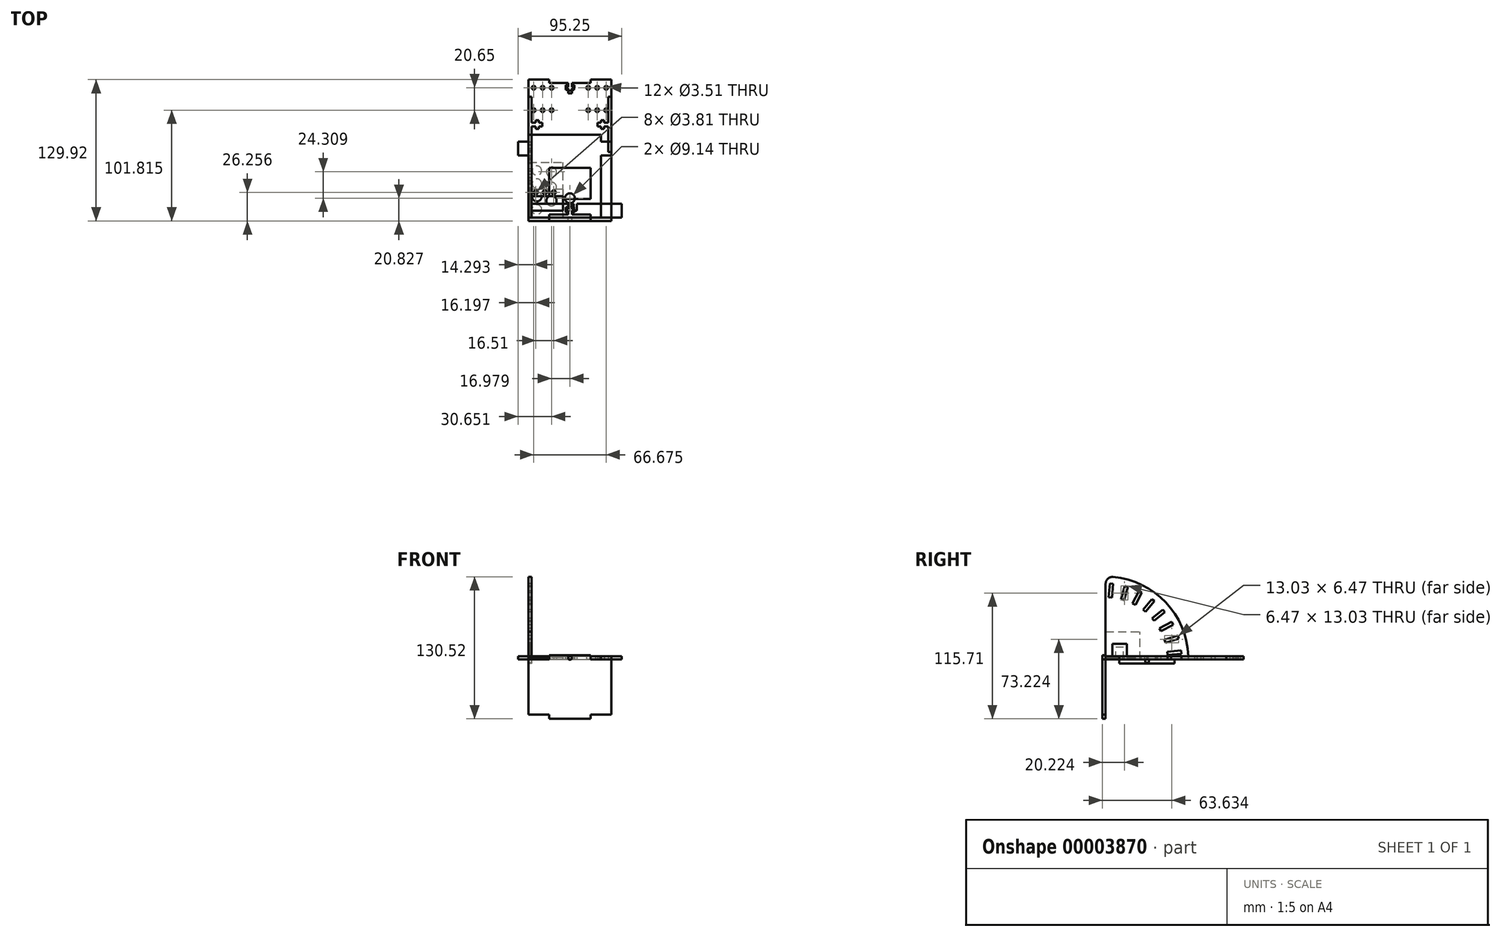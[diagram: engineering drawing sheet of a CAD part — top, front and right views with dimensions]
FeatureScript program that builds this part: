
annotation { "Feature Type Name" : "Feature", "Feature Type Description" : "" }
export const myFeature = defineFeature(function(context is Context, id is Id, definition is map)
    precondition{}
    {
        {
            var Q0;
            Q0=qCreatedBy(makeId("Right.planeOp"),FACE);
            var sketch = newSketch(context, id + "F0", { "sketchPlane" : qUnion([Q0])});
            skLineSegment(sketch, "E0", {"start": v(0, 0) * mm, "end": v(12.7, 0) * mm});
            skLineSegment(sketch, "E1", {"start": v(12.7, 0) * mm, "end": v(12.7, -3.81) * mm});
            skLineSegment(sketch, "E2", {"start": v(12.7, -3.81) * mm, "end": v(63.5, -3.81) * mm});
            skLineSegment(sketch, "E3", {"start": v(63.5, -3.81) * mm, "end": v(63.5, 0) * mm});
            skLineSegment(sketch, "E4", {"start": v(63.5, 0) * mm, "end": v(76.2, 0) * mm});
            skLineSegment(sketch, "E5", {"start": v(0, 0) * mm, "end": v(0, 69.56) * mm});
            skArc(sketch, "E6", {"start": v(76.2, 0) * mm, "mid": v(56.28, 51.37) * mm, "end": v(6.93, 75.88) * mm});
            skPoint(sketch, "E7.visualSharp", {"position": v(0, 76.2) * mm});
            skArc(sketch, "E7.filletArc", {"start": v(6.93, 75.88) * mm, "mid": v(2.07, 74.25) * mm, "end": v(0, 69.56) * mm});
            skSolve(sketch);
        }
        {
            var Q0;
            Q0=makeQuery(id+"F0.imprint","IMPRINT",FACE,{"disambiguationData":[TD([[makeQuery(id+"F0.imprint","IMPRINT",EDGE,{"derivedFrom":sQuery(id+"F0.wireOp",EDGE,"E0")}),1.0]])]});
            extrude(context, id + "F1", {"entities" : qUnion([Q0]), "depth" : 2.92 * mm});
        }
        {
            var Q0;
            Q0=qCreatedBy(makeId("Right.planeOp"),FACE);
            var sketch = newSketch(context, id + "F2", { "sketchPlane" : qUnion([Q0])});
            skLineSegment(sketch, "E8", {"start": v(56.74, 7.15) * mm, "end": v(69.4, 8.26) * mm});
            skLineSegment(sketch, "E9", {"start": v(69.4, 8.26) * mm, "end": v(69.66, 5.27) * mm});
            skLineSegment(sketch, "E10", {"start": v(69.66, 5.27) * mm, "end": v(57, 4.17) * mm});
            skLineSegment(sketch, "E11", {"start": v(57, 4.17) * mm, "end": v(56.74, 7.15) * mm});
            skLineSegment(sketch, "E12.1.0", {"start": v(54.2, 18.26) * mm, "end": v(66.38, 21.85) * mm});
            skLineSegment(sketch, "E12.1.1", {"start": v(66.38, 21.85) * mm, "end": v(67.23, 18.97) * mm});
            skLineSegment(sketch, "E12.1.2", {"start": v(67.23, 18.97) * mm, "end": v(55.05, 15.38) * mm});
            skLineSegment(sketch, "E12.1.3", {"start": v(55.05, 15.38) * mm, "end": v(54.2, 18.26) * mm});
            skLineSegment(sketch, "E12.2.0", {"start": v(49.5, 28.63) * mm, "end": v(60.74, 34.57) * mm});
            skLineSegment(sketch, "E12.2.1", {"start": v(60.74, 34.57) * mm, "end": v(62.14, 31.92) * mm});
            skLineSegment(sketch, "E12.2.2", {"start": v(62.14, 31.92) * mm, "end": v(50.9, 25.98) * mm});
            skLineSegment(sketch, "E12.2.3", {"start": v(50.9, 25.98) * mm, "end": v(49.5, 28.63) * mm});
            skLineSegment(sketch, "E12.3.0", {"start": v(42.85, 37.87) * mm, "end": v(52.68, 45.92) * mm});
            skLineSegment(sketch, "E12.3.1", {"start": v(52.68, 45.92) * mm, "end": v(54.58, 43.6) * mm});
            skLineSegment(sketch, "E12.3.2", {"start": v(54.58, 43.6) * mm, "end": v(44.75, 35.56) * mm});
            skLineSegment(sketch, "E12.3.3", {"start": v(44.75, 35.56) * mm, "end": v(42.85, 37.87) * mm});
            skLineSegment(sketch, "E12.4.0", {"start": v(34.5, 45.62) * mm, "end": v(42.54, 55.44) * mm});
            skLineSegment(sketch, "E12.4.1", {"start": v(42.54, 55.44) * mm, "end": v(44.86, 53.55) * mm});
            skLineSegment(sketch, "E12.4.2", {"start": v(44.86, 53.55) * mm, "end": v(36.82, 43.72) * mm});
            skLineSegment(sketch, "E12.4.3", {"start": v(36.82, 43.72) * mm, "end": v(34.5, 45.62) * mm});
            skLineSegment(sketch, "E12.5.0", {"start": v(24.78, 51.55) * mm, "end": v(30.71, 62.77) * mm});
            skLineSegment(sketch, "E12.5.1", {"start": v(30.71, 62.77) * mm, "end": v(33.36, 61.37) * mm});
            skLineSegment(sketch, "E12.5.2", {"start": v(33.36, 61.37) * mm, "end": v(27.43, 50.15) * mm});
            skLineSegment(sketch, "E12.5.3", {"start": v(27.43, 50.15) * mm, "end": v(24.78, 51.55) * mm});
            skLineSegment(sketch, "E12.6.0", {"start": v(14.07, 55.43) * mm, "end": v(17.66, 67.62) * mm});
            skLineSegment(sketch, "E12.6.1", {"start": v(17.66, 67.62) * mm, "end": v(20.54, 66.77) * mm});
            skLineSegment(sketch, "E12.6.2", {"start": v(20.54, 66.77) * mm, "end": v(16.95, 54.59) * mm});
            skLineSegment(sketch, "E12.6.3", {"start": v(16.95, 54.59) * mm, "end": v(14.07, 55.43) * mm});
            skLineSegment(sketch, "E12.7.0", {"start": v(2.8, 57.12) * mm, "end": v(3.91, 69.77) * mm});
            skLineSegment(sketch, "E12.7.1", {"start": v(3.91, 69.77) * mm, "end": v(6.9, 69.51) * mm});
            skLineSegment(sketch, "E12.7.2", {"start": v(6.9, 69.51) * mm, "end": v(5.8, 56.86) * mm});
            skLineSegment(sketch, "E12.7.3", {"start": v(5.8, 56.86) * mm, "end": v(2.8, 57.12) * mm});
            skPoint(sketch, "E12.center", {"position": v(0, 0) * mm});
            skLineSegment(sketch, "E12.anchor1", {"start": v(0, 0) * mm, "end": v(56.74, 7.15) * mm, "construction": true});
            skLineSegment(sketch, "E12.anchor2", {"start": v(0, 0) * mm, "end": v(2.8, 57.12) * mm, "construction": true});
            skCircle(sketch, "E13", {"center": v(0, 0) * mm, "radius": 69.85 * mm, "construction": true});
            skCircle(sketch, "E14", {"center": v(0, 0) * mm, "radius": 57.15 * mm, "construction": true});
            skCircle(sketch, "E15", {"center": v(38.1, -1.46) * mm, "radius": 1.75 * mm});
            skSolve(sketch);
        }
        {
            var Q0;
            {Q0=qUnion([makeQuery(id+"F2.imprint","IMPRINT",FACE,{"disambiguationData":[TD([[makeQuery(id+"F2.imprint","IMPRINT",EDGE,{"derivedFrom":sQuery(id+"F2.wireOp",EDGE,"E8")}),-1.0]])]}),makeQuery(id+"F2.imprint","IMPRINT",FACE,{"disambiguationData":[TD([[makeQuery(id+"F2.imprint","IMPRINT",EDGE,{"derivedFrom":sQuery(id+"F2.wireOp",EDGE,"E12.1.0")}),-1.0]])]}),makeQuery(id+"F2.imprint","IMPRINT",FACE,{"disambiguationData":[TD([[makeQuery(id+"F2.imprint","IMPRINT",EDGE,{"derivedFrom":sQuery(id+"F2.wireOp",EDGE,"E12.2.0")}),-1.0]])]}),makeQuery(id+"F2.imprint","IMPRINT",FACE,{"disambiguationData":[TD([[makeQuery(id+"F2.imprint","IMPRINT",EDGE,{"derivedFrom":sQuery(id+"F2.wireOp",EDGE,"E12.3.0")}),-1.0]])]}),makeQuery(id+"F2.imprint","IMPRINT",FACE,{"disambiguationData":[TD([[makeQuery(id+"F2.imprint","IMPRINT",EDGE,{"derivedFrom":sQuery(id+"F2.wireOp",EDGE,"E12.4.0")}),-1.0]])]}),makeQuery(id+"F2.imprint","IMPRINT",FACE,{"disambiguationData":[TD([[makeQuery(id+"F2.imprint","IMPRINT",EDGE,{"derivedFrom":sQuery(id+"F2.wireOp",EDGE,"E12.5.0")}),-1.0]])]}),makeQuery(id+"F2.imprint","IMPRINT",FACE,{"disambiguationData":[TD([[makeQuery(id+"F2.imprint","IMPRINT",EDGE,{"derivedFrom":sQuery(id+"F2.wireOp",EDGE,"E12.6.0")}),-1.0]])]}),makeQuery(id+"F2.imprint","IMPRINT",FACE,{"disambiguationData":[TD([[makeQuery(id+"F2.imprint","IMPRINT",EDGE,{"derivedFrom":sQuery(id+"F2.wireOp",EDGE,"E12.7.0")}),-1.0]])]}),makeQuery(id+"F2.imprint","IMPRINT",FACE,{"disambiguationData":[TD([[makeQuery(id+"F2.imprint","IMPRINT",EDGE,{"derivedFrom":sQuery(id+"F2.wireOp",EDGE,"E15")}),1.0]])]})]);}
            extrude(context, id + "F3", {"entities" : qUnion([Q0]), "operationType" : NewBodyOperationType.REMOVE, "depth" : 25.4 * mm});
        }
        {
            var Q0;
            Q0=qCreatedBy(makeId("Top.planeOp"),FACE);
            var sketch = newSketch(context, id + "F4", { "sketchPlane" : qUnion([Q0])});
            skLineSegment(sketch, "E16", {"start": v(0, 127) * mm, "end": v(0, 111.13) * mm});
            skLineSegment(sketch, "E17", {"start": v(0, 111.13) * mm, "end": v(2.92, 111.13) * mm});
            skLineSegment(sketch, "E18", {"start": v(2.92, 111.12) * mm, "end": v(2.92, 87.48) * mm});
            skLineSegment(sketch, "E19", {"start": v(2.92, 87.48) * mm, "end": v(6.75, 87.48) * mm});
            skLineSegment(sketch, "E20", {"start": v(6.75, 87.48) * mm, "end": v(6.75, 89.66) * mm});
            skLineSegment(sketch, "E21", {"start": v(6.75, 89.66) * mm, "end": v(9.53, 89.66) * mm});
            skLineSegment(sketch, "E22", {"start": v(9.53, 89.66) * mm, "end": v(9.53, 87.48) * mm});
            skLineSegment(sketch, "E23", {"start": v(9.53, 87.48) * mm, "end": v(12.7, 87.48) * mm});
            skLineSegment(sketch, "E24", {"start": v(12.7, 87.48) * mm, "end": v(12.7, 83.97) * mm});
            skLineSegment(sketch, "E25.0.MirrorCS", {"start": v(0, 60.33) * mm, "end": v(2.92, 60.33) * mm});
            skLineSegment(sketch, "E26.0.MirrorCS", {"start": v(2.92, 60.33) * mm, "end": v(2.92, 83.97) * mm});
            skLineSegment(sketch, "E27.0.MirrorCS", {"start": v(2.92, 83.97) * mm, "end": v(6.75, 83.97) * mm});
            skLineSegment(sketch, "E28.0.MirrorCS", {"start": v(6.75, 83.97) * mm, "end": v(6.75, 81.79) * mm});
            skLineSegment(sketch, "E29.0.MirrorCS", {"start": v(6.75, 81.79) * mm, "end": v(9.52, 81.79) * mm});
            skLineSegment(sketch, "E30.0.MirrorCS", {"start": v(9.52, 81.79) * mm, "end": v(9.52, 83.97) * mm});
            skLineSegment(sketch, "E31.0.MirrorCS", {"start": v(9.52, 83.97) * mm, "end": v(12.7, 83.97) * mm});
            skLineSegment(sketch, "E32.0.MirrorCS", {"start": v(76.2, 127) * mm, "end": v(76.2, 111.13) * mm});
            skLineSegment(sketch, "E33.0.MirrorCS", {"start": v(76.2, 111.13) * mm, "end": v(73.28, 111.13) * mm});
            skLineSegment(sketch, "E34.0.MirrorCS", {"start": v(73.28, 111.13) * mm, "end": v(73.28, 87.48) * mm});
            skLineSegment(sketch, "E35.0.MirrorCS", {"start": v(73.28, 87.48) * mm, "end": v(69.45, 87.48) * mm});
            skLineSegment(sketch, "E36.0.MirrorCS", {"start": v(69.45, 87.48) * mm, "end": v(69.45, 89.66) * mm});
            skLineSegment(sketch, "E37.0.MirrorCS", {"start": v(69.45, 89.66) * mm, "end": v(66.68, 89.66) * mm});
            skLineSegment(sketch, "E38.0.MirrorCS", {"start": v(66.67, 89.66) * mm, "end": v(66.67, 87.48) * mm});
            skLineSegment(sketch, "E39.0.MirrorCS", {"start": v(66.67, 87.48) * mm, "end": v(63.5, 87.48) * mm});
            skLineSegment(sketch, "E40.0.MirrorCS", {"start": v(63.5, 83.97) * mm, "end": v(63.5, 87.48) * mm});
            skLineSegment(sketch, "E41.0.MirrorCS", {"start": v(66.68, 83.97) * mm, "end": v(63.5, 83.97) * mm});
            skLineSegment(sketch, "E42.0.MirrorCS", {"start": v(66.68, 81.79) * mm, "end": v(66.68, 83.97) * mm});
            skLineSegment(sketch, "E43.0.MirrorCS", {"start": v(69.45, 81.79) * mm, "end": v(66.68, 81.79) * mm});
            skLineSegment(sketch, "E44.0.MirrorCS", {"start": v(69.45, 83.97) * mm, "end": v(69.45, 81.79) * mm});
            skLineSegment(sketch, "E45.0.MirrorCS", {"start": v(73.28, 83.97) * mm, "end": v(69.45, 83.97) * mm});
            skLineSegment(sketch, "E46.0.MirrorCS", {"start": v(73.28, 60.33) * mm, "end": v(73.28, 83.97) * mm});
            skLineSegment(sketch, "E47.0.MirrorCS", {"start": v(76.2, 60.33) * mm, "end": v(73.28, 60.33) * mm});
            skLineSegment(sketch, "E48", {"start": v(0, 0) * mm, "end": v(75.06, 0) * mm, "construction": true});
            skLineSegment(sketch, "E49", {"start": v(0, 127) * mm, "end": v(76.2, 127) * mm, "construction": true});
            skLineSegment(sketch, "E50", {"start": v(19.05, 0) * mm, "end": v(19.05, 2.92) * mm});
            skLineSegment(sketch, "E51", {"start": v(19.05, 2.92) * mm, "end": v(36.35, 2.92) * mm});
            skLineSegment(sketch, "E52", {"start": v(36.35, 2.92) * mm, "end": v(36.35, 6.75) * mm});
            skLineSegment(sketch, "E53", {"start": v(36.35, 6.75) * mm, "end": v(34.16, 6.75) * mm});
            skLineSegment(sketch, "E54", {"start": v(34.16, 6.75) * mm, "end": v(34.16, 9.53) * mm});
            skLineSegment(sketch, "E55", {"start": v(34.16, 9.53) * mm, "end": v(36.35, 9.53) * mm});
            skLineSegment(sketch, "E56", {"start": v(36.35, 9.53) * mm, "end": v(36.35, 12.7) * mm});
            skLineSegment(sketch, "E57.0.MirrorCS", {"start": v(57.15, 0) * mm, "end": v(57.15, 2.92) * mm});
            skLineSegment(sketch, "E58.0.MirrorCS", {"start": v(57.15, 2.92) * mm, "end": v(39.85, 2.92) * mm});
            skLineSegment(sketch, "E59.0.MirrorCS", {"start": v(39.85, 2.8) * mm, "end": v(39.85, 2.92) * mm});
            skLineSegment(sketch, "E60.0.MirrorCS", {"start": v(19.05, 127) * mm, "end": v(19.05, 124.08) * mm});
            skLineSegment(sketch, "E61.0.MirrorCS", {"start": v(19.05, 124.08) * mm, "end": v(36.35, 124.08) * mm});
            skLineSegment(sketch, "E62.0.MirrorCS", {"start": v(0, 127) * mm, "end": v(19.05, 127) * mm});
            skLineSegment(sketch, "E63.0.MirrorCS", {"start": v(36.35, 124.08) * mm, "end": v(36.35, 120.25) * mm});
            skLineSegment(sketch, "E64.0.MirrorCS", {"start": v(36.35, 120.25) * mm, "end": v(34.16, 120.25) * mm});
            skLineSegment(sketch, "E65.0.MirrorCS", {"start": v(34.16, 120.25) * mm, "end": v(34.16, 117.48) * mm});
            skLineSegment(sketch, "E66.0.MirrorCS", {"start": v(34.16, 117.48) * mm, "end": v(36.35, 117.48) * mm});
            skLineSegment(sketch, "E67.0.MirrorCS", {"start": v(36.35, 117.48) * mm, "end": v(36.35, 114.3) * mm});
            skLineSegment(sketch, "E68.0.MirrorCS", {"start": v(36.35, 114.3) * mm, "end": v(39.85, 114.3) * mm});
            skLineSegment(sketch, "E69.0.MirrorCS", {"start": v(39.85, 117.48) * mm, "end": v(39.85, 114.3) * mm});
            skLineSegment(sketch, "E70.0.MirrorCS", {"start": v(42.04, 117.48) * mm, "end": v(39.85, 117.48) * mm});
            skLineSegment(sketch, "E71.0.MirrorCS", {"start": v(42.04, 120.25) * mm, "end": v(42.04, 117.48) * mm});
            skLineSegment(sketch, "E72.0.MirrorCS", {"start": v(39.85, 120.25) * mm, "end": v(42.04, 120.25) * mm});
            skLineSegment(sketch, "E73.0.MirrorCS", {"start": v(39.85, 124.08) * mm, "end": v(39.85, 120.25) * mm});
            skLineSegment(sketch, "E74.0.MirrorCS", {"start": v(57.15, 124.08) * mm, "end": v(39.85, 124.08) * mm});
            skLineSegment(sketch, "E75.0.MirrorCS", {"start": v(57.15, 127) * mm, "end": v(57.15, 124.08) * mm});
            skLineSegment(sketch, "E76", {"start": v(57.15, 127) * mm, "end": v(76.2, 127) * mm});
            skLineSegment(sketch, "E77", {"start": v(39.85, 2.92) * mm, "end": v(39.85, 6.75) * mm});
            skLineSegment(sketch, "E78", {"start": v(39.85, 6.75) * mm, "end": v(42.04, 6.75) * mm});
            skLineSegment(sketch, "E79", {"start": v(42.04, 6.75) * mm, "end": v(42.04, 9.53) * mm});
            skLineSegment(sketch, "E80", {"start": v(42.04, 9.53) * mm, "end": v(39.85, 9.53) * mm});
            skLineSegment(sketch, "E81", {"start": v(39.85, 9.53) * mm, "end": v(39.85, 12.7) * mm});
            skLineSegment(sketch, "E82", {"start": v(39.85, 12.7) * mm, "end": v(36.35, 12.7) * mm});
            skLineSegment(sketch, "E83", {"start": v(76.2, 60.33) * mm, "end": v(76.2, 0) * mm});
            skLineSegment(sketch, "E84", {"start": v(76.2, 0) * mm, "end": v(57.15, 0) * mm});
            skLineSegment(sketch, "E85", {"start": v(19.05, 0) * mm, "end": v(0, 0) * mm});
            skLineSegment(sketch, "E86", {"start": v(0, 60.33) * mm, "end": v(0, 0) * mm});
            skLineSegment(sketch, "E87.bottom", {"start": v(19.05, 45.72) * mm, "end": v(57.15, 45.72) * mm});
            skLineSegment(sketch, "E87.top", {"start": v(19.05, 17.14) * mm, "end": v(57.15, 17.14) * mm});
            skLineSegment(sketch, "E87.left", {"start": v(19.05, 45.72) * mm, "end": v(19.05, 17.14) * mm});
            skLineSegment(sketch, "E87.right", {"start": v(57.15, 45.72) * mm, "end": v(57.15, 17.14) * mm});
            skSolve(sketch);
        }
        {
            var Q0;
            Q0 = qSketchRegion(id + "F4", true);
            extrude(context, id + "F5", {"entities" : qUnion([Q0]), "depth" : 2.92 * mm});
        }
        {
            var Q0;
            Q0=qCreatedBy(makeId("Top.planeOp"),FACE);
            var sketch = newSketch(context, id + "F6", { "sketchPlane" : qUnion([Q0])});
            skLineSegment(sketch, "E88", {"start": v(0, 0) * mm, "end": v(0, 57.15) * mm});
            skLineSegment(sketch, "E89", {"start": v(0, 57.15) * mm, "end": v(-9.53, 57.15) * mm});
            skLineSegment(sketch, "E90", {"start": v(-9.53, 57.15) * mm, "end": v(-9.53, 69.85) * mm});
            skLineSegment(sketch, "E91", {"start": v(-9.53, 69.85) * mm, "end": v(0, 69.85) * mm});
            skLineSegment(sketch, "E92", {"start": v(0, 69.85) * mm, "end": v(0, 76.2) * mm});
            skLineSegment(sketch, "E93", {"start": v(0, 76.2) * mm, "end": v(66.68, 76.2) * mm});
            skLineSegment(sketch, "E94", {"start": v(0, 0) * mm, "end": v(66.68, 0) * mm});
            skLineSegment(sketch, "E95", {"start": v(33.34, 93.53) * mm, "end": v(33.34, 0) * mm, "construction": true});
            skLineSegment(sketch, "E96.0.MirrorCS", {"start": v(66.68, 69.85) * mm, "end": v(66.68, 76.2) * mm});
            skLineSegment(sketch, "E97.0.MirrorCS", {"start": v(76.2, 69.85) * mm, "end": v(66.68, 69.85) * mm});
            skLineSegment(sketch, "E98.0.MirrorCS", {"start": v(76.2, 57.15) * mm, "end": v(76.2, 69.85) * mm});
            skLineSegment(sketch, "E99.0.MirrorCS", {"start": v(66.68, 57.15) * mm, "end": v(76.2, 57.15) * mm});
            skLineSegment(sketch, "E100.0.MirrorCS", {"start": v(66.68, 0) * mm, "end": v(66.68, 57.15) * mm});
            skSolve(sketch);
        }
        {
            var Q0;
            Q0=makeQuery(id+"F6.imprint","IMPRINT",FACE,{"disambiguationData":[TD([[makeQuery(id+"F6.imprint","IMPRINT",EDGE,{"derivedFrom":sQuery(id+"F6.wireOp",EDGE,"E88")}),-1.0]])]});
            extrude(context, id + "F7", {"entities" : qUnion([Q0]), "depth" : 2.92 * mm});
        }
        {
            var Q0;
            Q0=qCreatedBy(makeId("Front.planeOp"),FACE);
            var sketch = newSketch(context, id + "F8", { "sketchPlane" : qUnion([Q0])});
            skLineSegment(sketch, "E101", {"start": v(0, 0) * mm, "end": v(19.05, 0) * mm});
            skLineSegment(sketch, "E102", {"start": v(19.05, 0) * mm, "end": v(19.05, 3.81) * mm});
            skLineSegment(sketch, "E103", {"start": v(19.05, 3.81) * mm, "end": v(57.15, 3.81) * mm});
            skLineSegment(sketch, "E104", {"start": v(57.15, 3.81) * mm, "end": v(57.15, 0) * mm});
            skLineSegment(sketch, "E105", {"start": v(57.15, 0) * mm, "end": v(76.2, 0) * mm});
            skLineSegment(sketch, "E106", {"start": v(76.2, 0) * mm, "end": v(76.2, -50.8) * mm});
            skLineSegment(sketch, "E107", {"start": v(76.2, -50.8) * mm, "end": v(57.15, -50.8) * mm});
            skLineSegment(sketch, "E108", {"start": v(57.15, -50.8) * mm, "end": v(57.15, -54.6) * mm});
            skLineSegment(sketch, "E109", {"start": v(57.15, -54.6) * mm, "end": v(19.05, -54.6) * mm});
            skLineSegment(sketch, "E110", {"start": v(19.05, -54.6) * mm, "end": v(19.05, -50.8) * mm});
            skLineSegment(sketch, "E111", {"start": v(19.05, -50.8) * mm, "end": v(0, -50.8) * mm});
            skLineSegment(sketch, "E112", {"start": v(0, -50.8) * mm, "end": v(0, 0) * mm});
            skSolve(sketch);
        }
        {
            var Q0;
            Q0=makeQuery(id+"F8.imprint","IMPRINT",FACE,{"disambiguationData":[TD([[makeQuery(id+"F8.imprint","IMPRINT",EDGE,{"derivedFrom":sQuery(id+"F8.wireOp",EDGE,"E101")}),-1.0]])]});
            extrude(context, id + "F9", {"entities" : qUnion([Q0]), "depth" : 2.92 * mm});
        }
        {
            var Q0;
            Q0=qCreatedBy(makeId("Front.planeOp"),FACE);
            var sketch = newSketch(context, id + "F10", { "sketchPlane" : qUnion([Q0])});
            skCircle(sketch, "E113", {"center": v(38.1, 1.46) * mm, "radius": 1.75 * mm});
            skLineSegment(sketch, "E114", {"start": v(-12.64, -25.4) * mm, "end": v(76.2, -25.4) * mm, "construction": true});
            skCircle(sketch, "E115.0.MirrorC", {"center": v(38.1, -52.26) * mm, "radius": 1.75 * mm});
            skSolve(sketch);
        }
        {
            var Q0;
            {Q0=qUnion([makeQuery(id+"F10.imprint","IMPRINT",FACE,{"disambiguationData":[TD([[makeQuery(id+"F10.imprint","IMPRINT",EDGE,{"derivedFrom":sQuery(id+"F10.wireOp",EDGE,"E113")}),1.0]])]}),makeQuery(id+"F10.imprint","IMPRINT",FACE,{"disambiguationData":[TD([[makeQuery(id+"F10.imprint","IMPRINT",EDGE,{"derivedFrom":sQuery(id+"F10.wireOp",EDGE,"E115.0.MirrorC")}),-1.0]])]})]);}
            extrude(context, id + "F11", {"entities" : qUnion([Q0]), "operationType" : NewBodyOperationType.REMOVE, "depth" : 25.4 * mm});
        }
        {
            var Q0;
            Q0=qCreatedBy(makeId("Top.planeOp"),FACE);
            var sketch = newSketch(context, id + "F12", { "sketchPlane" : qUnion([Q0])});
            skLineSegment(sketch, "E116", {"start": v(0, 0) * mm, "end": v(19.05, 0) * mm});
            skLineSegment(sketch, "E117", {"start": v(19.05, 0) * mm, "end": v(19.05, 2.92) * mm});
            skLineSegment(sketch, "E118", {"start": v(19.05, 2.92) * mm, "end": v(36.35, 2.92) * mm});
            skLineSegment(sketch, "E119", {"start": v(36.35, 2.92) * mm, "end": v(36.35, 5) * mm});
            skLineSegment(sketch, "E120", {"start": v(36.35, 5) * mm, "end": v(34.13, 5) * mm});
            skLineSegment(sketch, "E121", {"start": v(34.13, 5) * mm, "end": v(34.13, 7.78) * mm});
            skLineSegment(sketch, "E122", {"start": v(34.13, 7.78) * mm, "end": v(36.35, 7.78) * mm});
            skLineSegment(sketch, "E123", {"start": v(36.35, 7.78) * mm, "end": v(36.35, 10.16) * mm});
            skLineSegment(sketch, "E124", {"start": v(36.35, 10.16) * mm, "end": v(38.1, 10.16) * mm});
            skLineSegment(sketch, "E125", {"start": v(0, 0) * mm, "end": v(0, 127) * mm});
            skLineSegment(sketch, "E126", {"start": v(38.1, 63.6) * mm, "end": v(38.1, -23.35) * mm, "construction": true});
            skLineSegment(sketch, "E127.0.MirrorCS", {"start": v(39.85, 10.16) * mm, "end": v(38.1, 10.16) * mm});
            skLineSegment(sketch, "E128.0.MirrorCS", {"start": v(39.85, 7.78) * mm, "end": v(39.85, 10.16) * mm});
            skLineSegment(sketch, "E129.0.MirrorCS", {"start": v(42.07, 7.78) * mm, "end": v(39.85, 7.78) * mm});
            skLineSegment(sketch, "E130.0.MirrorCS", {"start": v(42.07, 5) * mm, "end": v(42.07, 7.78) * mm});
            skLineSegment(sketch, "E131.0.MirrorCS", {"start": v(39.85, 5) * mm, "end": v(42.07, 5) * mm});
            skLineSegment(sketch, "E132.0.MirrorCS", {"start": v(39.85, 2.92) * mm, "end": v(39.85, 5) * mm});
            skLineSegment(sketch, "E133.0.MirrorCS", {"start": v(57.15, 2.92) * mm, "end": v(39.85, 2.92) * mm});
            skLineSegment(sketch, "E134.0.MirrorCS", {"start": v(57.15, 0) * mm, "end": v(57.15, 2.92) * mm});
            skLineSegment(sketch, "E135.0.MirrorCS", {"start": v(76.2, 0) * mm, "end": v(57.15, 0) * mm});
            skLineSegment(sketch, "E136.0.MirrorCS", {"start": v(76.2, 0) * mm, "end": v(76.2, 127) * mm});
            skLineSegment(sketch, "E137", {"start": v(0, 127) * mm, "end": v(19.05, 127) * mm});
            skLineSegment(sketch, "E138", {"start": v(19.05, 127) * mm, "end": v(19.05, 124.08) * mm});
            skLineSegment(sketch, "E139", {"start": v(19.05, 124.08) * mm, "end": v(36.35, 124.08) * mm});
            skLineSegment(sketch, "E140", {"start": v(36.35, 124.08) * mm, "end": v(36.35, 122) * mm});
            skLineSegment(sketch, "E141", {"start": v(36.35, 122) * mm, "end": v(34.13, 122) * mm});
            skLineSegment(sketch, "E142", {"start": v(34.13, 122) * mm, "end": v(34.13, 119.22) * mm});
            skLineSegment(sketch, "E143", {"start": v(34.13, 119.22) * mm, "end": v(36.35, 119.22) * mm});
            skLineSegment(sketch, "E144", {"start": v(36.35, 119.22) * mm, "end": v(36.35, 116.84) * mm});
            skLineSegment(sketch, "E145", {"start": v(36.35, 116.84) * mm, "end": v(38.1, 116.84) * mm});
            skLineSegment(sketch, "E146", {"start": v(38.1, 116.84) * mm, "end": v(39.85, 116.84) * mm});
            skLineSegment(sketch, "E147", {"start": v(39.85, 116.84) * mm, "end": v(39.85, 119.22) * mm});
            skLineSegment(sketch, "E148", {"start": v(39.85, 119.22) * mm, "end": v(42.07, 119.22) * mm});
            skLineSegment(sketch, "E149", {"start": v(42.07, 119.22) * mm, "end": v(42.07, 122) * mm});
            skLineSegment(sketch, "E150", {"start": v(42.07, 122) * mm, "end": v(39.85, 122) * mm});
            skLineSegment(sketch, "E151", {"start": v(39.85, 122) * mm, "end": v(39.85, 124.08) * mm});
            skLineSegment(sketch, "E152", {"start": v(39.85, 124.08) * mm, "end": v(57.15, 124.08) * mm});
            skLineSegment(sketch, "E153", {"start": v(57.15, 124.08) * mm, "end": v(57.15, 127) * mm});
            skLineSegment(sketch, "E154", {"start": v(57.15, 127) * mm, "end": v(76.2, 127) * mm});
            skCircle(sketch, "E155", {"center": v(71.44, 119.55) * mm, "radius": 1.75 * mm});
            skCircle(sketch, "E156", {"center": v(71.44, 98.9) * mm, "radius": 1.75 * mm});
            skLineSegment(sketch, "E157", {"start": v(71.44, 119.55) * mm, "end": v(71.44, 98.9) * mm, "construction": true});
            skLineSegment(sketch, "E158", {"start": v(76.2, 109.22) * mm, "end": v(71.44, 109.22) * mm, "construction": true});
            skCircle(sketch, "E159.1.0.0", {"center": v(63.18, 119.55) * mm, "radius": 1.75 * mm});
            skCircle(sketch, "E159.1.0.1", {"center": v(63.18, 98.9) * mm, "radius": 1.75 * mm});
            skCircle(sketch, "E159.2.0.0", {"center": v(54.93, 119.55) * mm, "radius": 1.75 * mm});
            skCircle(sketch, "E159.2.0.1", {"center": v(54.93, 98.9) * mm, "radius": 1.75 * mm});
            skLineSegment(sketch, "E159.direction1", {"start": v(71.44, 119.55) * mm, "end": v(63.18, 119.55) * mm, "construction": true});
            skCircle(sketch, "E160.0.MirrorC", {"center": v(21.27, 119.55) * mm, "radius": 1.75 * mm});
            skCircle(sketch, "E161.0.MirrorC", {"center": v(13.02, 119.55) * mm, "radius": 1.75 * mm});
            skCircle(sketch, "E162.0.MirrorC", {"center": v(4.76, 119.55) * mm, "radius": 1.75 * mm});
            skCircle(sketch, "E163.0.MirrorC", {"center": v(4.76, 98.9) * mm, "radius": 1.75 * mm});
            skCircle(sketch, "E164.0.MirrorC", {"center": v(13.02, 98.9) * mm, "radius": 1.75 * mm});
            skCircle(sketch, "E165.0.MirrorC", {"center": v(21.27, 98.9) * mm, "radius": 1.75 * mm});
            skCircle(sketch, "E166", {"center": v(38.1, 17.9) * mm, "radius": 4.57 * mm});
            skSolve(sketch);
        }
        {
            var Q0;
            Q0 = qSketchRegion(id + "F12", true);
            extrude(context, id + "F13", {"entities" : qUnion([Q0]), "depth" : 2.92 * mm});
        }
        {
            var Q0;
            Q0=qCreatedBy(makeId("Right.planeOp"),FACE);
            var sketch = newSketch(context, id + "F14", { "sketchPlane" : qUnion([Q0])});
            skLineSegment(sketch, "E167", {"start": v(0, 1.59) * mm, "end": v(6.35, 1.59) * mm});
            skLineSegment(sketch, "E168", {"start": v(6.35, 1.59) * mm, "end": v(6.35, 14.29) * mm});
            skLineSegment(sketch, "E169", {"start": v(6.35, 14.29) * mm, "end": v(19.68, 14.29) * mm});
            skLineSegment(sketch, "E170", {"start": v(19.68, 14.29) * mm, "end": v(19.69, 1.59) * mm});
            skLineSegment(sketch, "E171", {"start": v(19.69, 1.59) * mm, "end": v(26.04, 1.59) * mm});
            skLineSegment(sketch, "E172", {"start": v(26.04, 1.59) * mm, "end": v(26.04, 0) * mm});
            skLineSegment(sketch, "E173", {"start": v(26.04, 0) * mm, "end": v(0, 0) * mm});
            skLineSegment(sketch, "E174", {"start": v(0, 0) * mm, "end": v(0, 1.59) * mm});
            skSolve(sketch);
        }
        {
            var Q0;
            Q0=makeQuery(id+"F14.imprint","IMPRINT",FACE,{"disambiguationData":[TD([[makeQuery(id+"F14.imprint","IMPRINT",EDGE,{"derivedFrom":sQuery(id+"F14.wireOp",EDGE,"E167")}),-1.0]])]});
            extrude(context, id + "F15", {"entities" : qUnion([Q0]), "depth" : (0.97 + (1 / 8)) * mm});
        }
        {
            var Q0;
            Q0=qCreatedBy(makeId("Top.planeOp"),FACE);
            var sketch = newSketch(context, id + "F16", { "sketchPlane" : qUnion([Q0])});
            skLineSegment(sketch, "E175.bottom", {"start": v(1.59, 18.1) * mm, "end": v(26.35, 18.1) * mm});
            skLineSegment(sketch, "E175.top", {"start": v(1.59, 7.94) * mm, "end": v(26.35, 7.94) * mm});
            skLineSegment(sketch, "E175.left", {"start": v(1.59, 18.1) * mm, "end": v(1.59, 7.94) * mm});
            skLineSegment(sketch, "E175.right", {"start": v(26.35, 18.1) * mm, "end": v(26.35, 7.94) * mm});
            skSolve(sketch);
        }
        {
            var Q0;
            Q0=makeQuery(id+"F16.imprint","IMPRINT",FACE,{"disambiguationData":[TD([[makeQuery(id+"F16.imprint","IMPRINT",EDGE,{"derivedFrom":sQuery(id+"F16.wireOp",EDGE,"E175.bottom")}),-1.0]])]});
            extrude(context, id + "F17", {"entities" : qUnion([Q0]), "operationType" : NewBodyOperationType.REMOVE, "depth" : 12.7 * mm});
        }
        {
            var Q0;
            Q0=qCreatedBy(makeId("Right.planeOp"),FACE);
            var sketch = newSketch(context, id + "F18", { "sketchPlane" : qUnion([Q0])});
            skLineSegment(sketch, "E176", {"start": v(11.11, 0) * mm, "end": v(14.92, 0) * mm});
            skLineSegment(sketch, "E177", {"start": v(14.92, 0) * mm, "end": v(14.92, 6.35) * mm});
            skLineSegment(sketch, "E178", {"start": v(11.11, 0) * mm, "end": v(11.11, 6.35) * mm});
            skArc(sketch, "E179", {"start": v(11.11, 6.35) * mm, "mid": v(13.02, 8.26) * mm, "end": v(14.92, 6.35) * mm});
            skLineSegment(sketch, "E180", {"start": v(6.35, 6.35) * mm, "end": v(19.69, 6.35) * mm, "construction": true});
            skLineSegment(sketch, "E181", {"start": v(4.37, 8.26) * mm, "end": v(24.9, 8.26) * mm, "construction": true});
            skSolve(sketch);
        }
        {
            var Q0;
            Q0=makeQuery(id+"F18.imprint","IMPRINT",FACE,{"disambiguationData":[TD([[makeQuery(id+"F18.imprint","IMPRINT",EDGE,{"derivedFrom":sQuery(id+"F18.wireOp",EDGE,"E176")}),1.0]])]});
            var Q1;
            Q1=makeQuery(id+"F15.opExtrude","CAP_FACE",FACE,{"disambiguationData":[OSD([sQuery(id+"F14.wireOp",EDGE,"E167"),sQuery(id+"F14.wireOp",EDGE,"E168"),sQuery(id+"F14.wireOp",EDGE,"E169"),sQuery(id+"F14.wireOp",EDGE,"E170"),sQuery(id+"F14.wireOp",EDGE,"E171"),sQuery(id+"F14.wireOp",EDGE,"E172"),sQuery(id+"F14.wireOp",EDGE,"E173"),sQuery(id+"F14.wireOp",EDGE,"E174")])],"isStart":false});
            extrude(context, id + "F19", {"entities" : qUnion([Q0, Q1]), "operationType" : NewBodyOperationType.REMOVE, "depth" : 30.48 * mm});
        }
        {
            var Q0;
            Q0=qCreatedBy(makeId("Top.planeOp"),FACE);
            var sketch = newSketch(context, id + "F20", { "sketchPlane" : qUnion([Q0])});
            skCircle(sketch, "E182", {"center": v(23.18, 23.34) * mm, "radius": 1.9 * mm});
            skLineSegment(sketch, "E183", {"start": v(0, 23.34) * mm, "end": v(27.94, 23.34) * mm, "construction": true});
            skLineSegment(sketch, "E184", {"start": v(0, 13.02) * mm, "end": v(25.48, 13.02) * mm, "construction": true});
            skCircle(sketch, "E185.0.MirrorC", {"center": v(23.18, 2.7) * mm, "radius": 1.9 * mm});
            skCircle(sketch, "E186.1.0.0", {"center": v(14.92, 23.34) * mm, "radius": 1.9 * mm});
            skCircle(sketch, "E186.1.0.1", {"center": v(14.92, 2.7) * mm, "radius": 1.9 * mm});
            skCircle(sketch, "E186.2.0.0", {"center": v(6.67, 23.34) * mm, "radius": 1.9 * mm});
            skCircle(sketch, "E186.2.0.1", {"center": v(6.67, 2.7) * mm, "radius": 1.9 * mm});
            skLineSegment(sketch, "E186.direction1", {"start": v(23.18, 23.34) * mm, "end": v(14.92, 23.34) * mm, "construction": true});
            skSolve(sketch);
        }
        {
            var Q0;
            {Q0=qUnion([makeQuery(id+"F20.imprint","IMPRINT",FACE,{"disambiguationData":[TD([[makeQuery(id+"F20.imprint","IMPRINT",EDGE,{"derivedFrom":sQuery(id+"F20.wireOp",EDGE,"E182")}),1.0]])]}),makeQuery(id+"F20.imprint","IMPRINT",FACE,{"disambiguationData":[TD([[makeQuery(id+"F20.imprint","IMPRINT",EDGE,{"derivedFrom":sQuery(id+"F20.wireOp",EDGE,"E185.0.MirrorC")}),-1.0]])]}),makeQuery(id+"F20.imprint","IMPRINT",FACE,{"disambiguationData":[TD([[makeQuery(id+"F20.imprint","IMPRINT",EDGE,{"derivedFrom":sQuery(id+"F20.wireOp",EDGE,"E186.1.0.0")}),1.0]])]}),makeQuery(id+"F20.imprint","IMPRINT",FACE,{"disambiguationData":[TD([[makeQuery(id+"F20.imprint","IMPRINT",EDGE,{"derivedFrom":sQuery(id+"F20.wireOp",EDGE,"E186.1.0.1")}),-1.0]])]}),makeQuery(id+"F20.imprint","IMPRINT",FACE,{"disambiguationData":[TD([[makeQuery(id+"F20.imprint","IMPRINT",EDGE,{"derivedFrom":sQuery(id+"F20.wireOp",EDGE,"E186.2.0.0")}),1.0]])]}),makeQuery(id+"F20.imprint","IMPRINT",FACE,{"disambiguationData":[TD([[makeQuery(id+"F20.imprint","IMPRINT",EDGE,{"derivedFrom":sQuery(id+"F20.wireOp",EDGE,"E186.2.0.1")}),-1.0]])]})]);}
            extrude(context, id + "F21", {"entities" : qUnion([Q0]), "operationType" : NewBodyOperationType.REMOVE, "depth" : 25.4 * mm});
        }
        {
            var Q0;
            Q0=qCreatedBy(makeId("Right.planeOp"),FACE);
            var sketch = newSketch(context, id + "F22", { "sketchPlane" : qUnion([Q0])});
            skLineSegment(sketch, "E187.bottom", {"start": v(9.52, 11.11) * mm, "end": v(16.51, 11.11) * mm});
            skLineSegment(sketch, "E187.top", {"start": v(9.52, 0) * mm, "end": v(16.51, 0) * mm});
            skLineSegment(sketch, "E187.left", {"start": v(9.52, 11.11) * mm, "end": v(9.52, 0) * mm});
            skLineSegment(sketch, "E187.right", {"start": v(16.51, 11.11) * mm, "end": v(16.51, 0) * mm});
            skSolve(sketch);
        }
        {
            var Q0;
            Q0=makeQuery(id+"F22.imprint","IMPRINT",FACE,{"disambiguationData":[TD([[makeQuery(id+"F22.imprint","IMPRINT",EDGE,{"derivedFrom":sQuery(id+"F22.wireOp",EDGE,"E187.bottom")}),-1.0]])]});
            extrude(context, id + "F23", {"entities" : qUnion([Q0]), "operationType" : NewBodyOperationType.REMOVE, "depth" : 5.17 * mm});
        }
        {
            var Q0;
            Q0=qCreatedBy(makeId("Top.planeOp"),FACE);
            var sketch = newSketch(context, id + "F24", { "sketchPlane" : qUnion([Q0])});
            skLineSegment(sketch, "E188.bottom", {"start": v(0, 0) * mm, "end": v(31.75, 0) * mm});
            skLineSegment(sketch, "E188.top", {"start": v(0, 50.8) * mm, "end": v(31.75, 50.8) * mm});
            skLineSegment(sketch, "E188.left", {"start": v(0, 0) * mm, "end": v(0, 50.8) * mm});
            skLineSegment(sketch, "E188.right", {"start": v(31.75, 0) * mm, "end": v(31.75, 50.8) * mm});
            skCircle(sketch, "E189", {"center": v(7.67, 19.43) * mm, "radius": 4.45 * mm});
            skCircle(sketch, "E190", {"center": v(7.67, 7.5) * mm, "radius": 4.5 * mm});
            skCircle(sketch, "E191", {"center": v(21.12, 42.22) * mm, "radius": 4.57 * mm});
            skCircle(sketch, "E192", {"center": v(21.12, 27.96) * mm, "radius": 4.64 * mm});
            skCircle(sketch, "E193", {"center": v(21.12, 15.58) * mm, "radius": 4.7 * mm});
            skCircle(sketch, "E194", {"center": v(7.67, 31.43) * mm, "radius": 4.38 * mm});
            skCircle(sketch, "E195", {"center": v(7.67, 43.3) * mm, "radius": 4.32 * mm});
            skLineSegment(sketch, "E196", {"start": v(7.67, 50.8) * mm, "end": v(7.67, 0) * mm, "construction": true});
            skLineSegment(sketch, "E197", {"start": v(21.12, 50.8) * mm, "end": v(21.12, 0) * mm, "construction": true});
            skSolve(sketch);
        }
        {
            var Q0;
            Q0 = qSketchRegion(id + "F24", true);
            extrude(context, id + "F25", {"entities" : qUnion([Q0]), "depth" : 2.8 * mm});
        }
        {
            var Q0;
            Q0=qCreatedBy(makeId("Top.planeOp"),FACE);
            var sketch = newSketch(context, id + "F26", { "sketchPlane" : qUnion([Q0])});
            skLineSegment(sketch, "E198", {"start": v(0, 0) * mm, "end": v(0, 12.7) * mm});
            skLineSegment(sketch, "E199", {"start": v(85.73, 12.7) * mm, "end": v(85.73, 0) * mm});
            skLineSegment(sketch, "E200", {"start": v(85.73, 0) * mm, "end": v(0, 0) * mm});
            skLineSegment(sketch, "E201", {"start": v(-9.52, 69.85) * mm, "end": v(76.2, 69.85) * mm, "construction": true});
            skLineSegment(sketch, "E202", {"start": v(0, 12.7) * mm, "end": v(41.41, 12.7) * mm});
            skLineSegment(sketch, "E203", {"start": v(41.41, 12.7) * mm, "end": v(41.41, 6.35) * mm});
            skLineSegment(sketch, "E204", {"start": v(41.41, 6.35) * mm, "end": v(44.31, 6.35) * mm});
            skLineSegment(sketch, "E205", {"start": v(44.31, 6.35) * mm, "end": v(44.31, 12.7) * mm});
            skLineSegment(sketch, "E206", {"start": v(44.31, 12.7) * mm, "end": v(85.73, 12.7) * mm});
            skSolve(sketch);
        }
        {
            var Q0;
            Q0 = qSketchRegion(id + "F26", true);
            extrude(context, id + "F27", {"entities" : qUnion([Q0]), "depth" : 2.92 * mm});
        }
        {
            var Q0;
            Q0=qCreatedBy(makeId("Right.planeOp"),FACE);
            var sketch = newSketch(context, id + "F28", { "sketchPlane" : qUnion([Q0])});
            skLineSegment(sketch, "E207.bottom", {"start": v(0, 0) * mm, "end": v(31.75, 0) * mm});
            skLineSegment(sketch, "E207.top", {"start": v(0, 25.4) * mm, "end": v(31.75, 25.4) * mm});
            skLineSegment(sketch, "E207.left", {"start": v(0, 0) * mm, "end": v(0, 25.4) * mm});
            skLineSegment(sketch, "E207.right", {"start": v(31.75, 0) * mm, "end": v(31.75, 25.4) * mm});
            skSolve(sketch);
        }
        {
            var Q0;
            Q0 = qSketchRegion(id + "F28", true);
            extrude(context, id + "F29", {"entities" : qUnion([Q0]), "depth" : 2.9 * mm});
        }
    });
